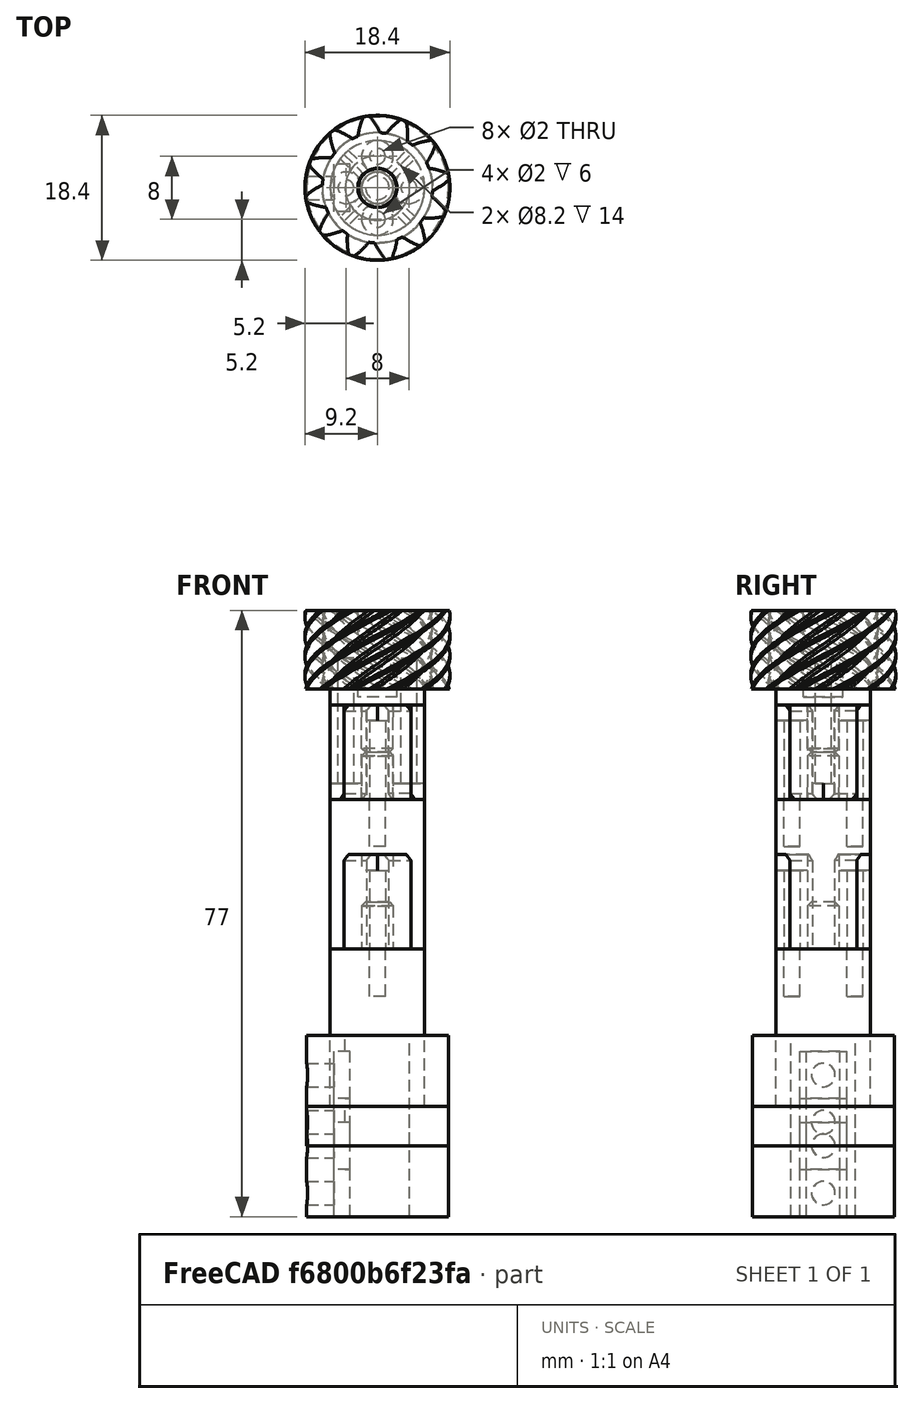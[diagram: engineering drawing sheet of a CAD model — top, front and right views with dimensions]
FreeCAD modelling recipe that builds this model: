
FCSTD DOCUMENT  (FreeCAD 0.19R24276 (Git))
Label: G-midi_inner-gear_002
License: All rights reserved
LicenseURL: http://en.wikipedia.org/wiki/All_rights_reserved
objects: Part::Cylinder×32, Part::Cut×26, Part::Compound×17, Part::Box×10, Part::Chamfer×6, Part::FeaturePython×3
note: 94 computed .brp shape members not serialized (recipe doc carries the construction recipe); baked Part::Feature solids carry a one-line shape summary decoded from their .brp

FEATURE [Part::Cylinder] Cylinder1841  label="Válec1841"
  Angle = 360
  AttacherType = Attacher::AttachEngine3D
  Height = 6
  Placement = pos=(0,0,-14) rot=(0,0,1;0rad)
  Radius = 2
FEATURE [Part::Cylinder] Cylinder1838  label="Válec1838"
  Angle = 360
  AttacherType = Attacher::AttachEngine3D
  Height = 12
  Placement = pos=(0,0,-20) rot=(0,0,1;0rad)
  Radius = 2
FEATURE [Part::Cylinder] Cylinder1839  label="Válec1839"
  Angle = 360
  AttacherType = Attacher::AttachEngine3D
  Height = 12
  Placement = pos=(0,0,-20) rot=(0,0,1;0rad)
  Radius = 6
FEATURE [Part::Cut] Cut392
  Base = -> Cylinder1839
  Tool = -> Cylinder1838
FEATURE [Part::Box] Box369  label="Krychle369"
  AttacherType = Attacher::AttachEngine3D
  Height = 12
  Length = 16
  Placement = pos=(-5.65685,-5.65685,-20) rot=(0,0,1;0.785398rad)
  Width = 8
FEATURE [Part::Cylinder] Cylinder1840  label="Válec1840"
  Angle = 360
  AttacherType = Attacher::AttachEngine3D
  Height = 20
  Placement = pos=(4,0,-20) rot=(0,0,-1;1.5708rad)
  Radius = 1
FEATURE [Part::Box] Box370  label="Krychle370"
  AttacherType = Attacher::AttachEngine3D
  Height = 12
  Length = 16
  Placement = pos=(5.65685,-5.65685,-20) rot=(0,0,1;2.35619rad)
  Width = 8
FEATURE [Part::Cut] Cut393
  Base = -> Cut392
  Tool = -> Box370
FEATURE [Part::Cut] Cut394
  Base = -> Cut393
  Tool = -> Box369
FEATURE [Part::Cut] Cut395
  Base = -> Cut394
  Tool = -> Cylinder1840
FEATURE [Part::Cut] Cut396
  Base = -> Cut394
  Placement = pos=(0,0,0) rot=(0,0,1;3.14159rad)
  Tool = -> Cylinder1840
FEATURE [Part::Compound] Compound584  label="G-midi_sun-sym-mixo"
  Links = -> [Cut395,Cut396,Cylinder1841]
  Placement = pos=(0,0,26) rot=(0,0,1;0rad)
FEATURE [Part::FeaturePython] wormgear061  # WARN: FeaturePython — macro-defined, semantics opaque (R4)
  AttacherType = Attacher::AttachEngine3D
  Placement = pos=(0,0,20) rot=(0,0,1;0.881391rad)
  beta = 30.9638
  clearance = 0.25
  diameter = 16
  head = 0.5
  height = 10
  module = 0.8
  pressure_angle = 20
  reverse_pitch = false
  teeth = 12
  version = 0.0.3
FEATURE [Part::Cylinder] Cylinder  label="Válec"
  Angle = 360
  AttacherType = Attacher::AttachEngine3D
  Height = 2
  Placement = pos=(0,0,18) rot=(0,0,1;0rad)
  Radius = 6
FEATURE [Part::Cylinder] Cylinder031  label="Válec031"
  Angle = 360
  AttacherType = Attacher::AttachEngine3D
  Height = 11
  Placement = pos=(0,0,19) rot=(0,0,1;0rad)
  Radius = 2.5
FEATURE [Part::Compound] Compound
  Links = -> [wormgear061,Cylinder]
FEATURE [Part::Cut] Cut
  Base = -> Compound
  Tool = -> Cylinder031
FEATURE [Part::Cylinder] Cylinder1842  label="Válec1842"
  Angle = 360
  AttacherType = Attacher::AttachEngine3D
  Height = 2
  Placement = pos=(4,0,-20) rot=(0,0,-1;1.5708rad)
  Radius = 2
FEATURE [Part::Cylinder] Cylinder1843  label="Válec1843"
  Angle = 360
  AttacherType = Attacher::AttachEngine3D
  Height = 2
  Placement = pos=(-4,0,-20) rot=(0,0,-1;1.5708rad)
  Radius = 2
FEATURE [Part::Cylinder] Cylinder1844  label="Válec1844"
  Angle = 360
  AttacherType = Attacher::AttachEngine3D
  Height = 20
  Placement = pos=(4,0,-20) rot=(0,0,-1;1.5708rad)
  Radius = 1
FEATURE [Part::Cylinder] Cylinder1845  label="Válec1845"
  Angle = 360
  AttacherType = Attacher::AttachEngine3D
  Height = 20
  Placement = pos=(-4,0,-20) rot=(0,0,-1;1.5708rad)
  Radius = 1
FEATURE [Part::Compound] Compound585
  Links = -> [Cylinder1842,Cylinder1843]
  Placement = pos=(0,0,26) rot=(0,0,1;0rad)
FEATURE [Part::Chamfer] Chamfer
  Base = -> Compound584
  Edges = 4 edges r=0.75: [Edge8,Edge11,Edge29,Edge32]
FEATURE [Part::Cut] Cut397
  Base = -> Chamfer
  Tool = -> Compound585
FEATURE [Part::Compound] Compound586
  Links = -> [Cylinder1844,Cylinder1845]
  Placement = pos=(0,0,24) rot=(0,0,1;0rad)
FEATURE [Part::Cut] Cut398
  Base = -> Cut
  Tool = -> Compound586
FEATURE [Part::Chamfer] Chamfer001
  Base = -> Cut397
  Edges = 1 edges r=0.5: [Edge75]
FEATURE [Part::Compound] Compound587  label="G-midi_inner-gear-part-A"
  Links = -> [Cut398,Chamfer001]
FEATURE [Part::FeaturePython] Tube094  # WARN: FeaturePython — macro-defined, semantics opaque (R4)
  AttacherType = Attacher::AttachEngine3D
  Height = 14
  InnerRadius = 4.1
  OuterRadius = 9
  Placement = pos=(0,0,-100) rot=(0,0,1;0rad)
FEATURE [Part::Cylinder] Cylinder751  label="Válec751"
  Angle = 360
  AttacherType = Attacher::AttachEngine3D
  Height = 10
  Placement = pos=(-11,0,-91) rot=(0.57735,0.57735,0.57735;2.0944rad)
  Radius = 1.5
FEATURE [Part::Cylinder] Cylinder752  label="Válec752"
  Angle = 360
  AttacherType = Attacher::AttachEngine3D
  Height = 10
  Placement = pos=(-11,0,-97) rot=(0.57735,0.57735,0.57735;2.0944rad)
  Radius = 1.5
FEATURE [Part::Compound] Compound533
  Links = -> [Cylinder751,Cylinder752]
FEATURE [Part::Box] Box313  label="Krychle313"
  AttacherType = Attacher::AttachEngine3D
  Height = 6
  Length = 6
  Placement = pos=(-3.5,-3,-100) rot=(0,0,1;1.5708rad)
  Width = 2
FEATURE [Part::Box] Box314  label="Krychle314"
  AttacherType = Attacher::AttachEngine3D
  Height = 6
  Length = 6
  Placement = pos=(-3.5,-3,-94) rot=(0,0,1;1.5708rad)
  Width = 2
FEATURE [Part::Compound] Compound532
  Links = -> [Box313,Box314]
FEATURE [Part::Cut] Cut303
  Base = -> Tube094
  Tool = -> Compound532
FEATURE [Part::Cut] Cut304
  Base = -> Cut303
  Placement = pos=(0,0,53) rot=(0,0,1;0rad)
  Tool = -> Compound533
FEATURE [Part::Cylinder] Cylinder754  label="Válec754"
  Angle = 360
  AttacherType = Attacher::AttachEngine3D
  Height = 20
  Placement = pos=(0,0,-33) rot=(0,0,1;0rad)
  Radius = 6
FEATURE [Part::Cylinder] Cylinder1846  label="Válec1846"
  Angle = 360
  AttacherType = Attacher::AttachEngine3D
  Height = 12
  Placement = pos=(0,0,-20) rot=(0,0,1;0rad)
  Radius = 2
FEATURE [Part::Cylinder] Cylinder1847  label="Válec1847"
  Angle = 360
  AttacherType = Attacher::AttachEngine3D
  Height = 6
  Placement = pos=(0,0,-14) rot=(0,0,1;0rad)
  Radius = 2
FEATURE [Part::Box] Box371  label="Krychle371"
  AttacherType = Attacher::AttachEngine3D
  Height = 12
  Length = 16
  Placement = pos=(-5.65685,-5.65685,-20) rot=(0,0,1;0.785398rad)
  Width = 8
FEATURE [Part::Cylinder] Cylinder1848  label="Válec1848"
  Angle = 360
  AttacherType = Attacher::AttachEngine3D
  Height = 20
  Placement = pos=(4,0,-20) rot=(0,0,-1;1.5708rad)
  Radius = 1
FEATURE [Part::Box] Box372  label="Krychle372"
  AttacherType = Attacher::AttachEngine3D
  Height = 12
  Length = 16
  Placement = pos=(5.65685,-5.65685,-20) rot=(0,0,1;2.35619rad)
  Width = 8
FEATURE [Part::Cylinder] Cylinder1849  label="Válec1849"
  Angle = 360
  AttacherType = Attacher::AttachEngine3D
  Height = 12
  Placement = pos=(0,0,-20) rot=(0,0,1;0rad)
  Radius = 6
FEATURE [Part::Cut] Cut400
  Base = -> Cylinder1849
  Tool = -> Cylinder1846
FEATURE [Part::Cut] Cut404
  Base = -> Cut400
  Tool = -> Box372
FEATURE [Part::Cut] Cut401
  Base = -> Cut404
  Tool = -> Box371
FEATURE [Part::Cut] Cut402
  Base = -> Cut401
  Tool = -> Cylinder1848
FEATURE [Part::Cut] Cut403
  Base = -> Cut401
  Placement = pos=(0,0,0) rot=(0,0,1;3.14159rad)
  Tool = -> Cylinder1848
FEATURE [Part::Compound] Compound588  label="G-midi_sun-sym-mixo001"
  Links = -> [Cut402,Cut403,Cylinder1847]
  Placement = pos=(0,0,26) rot=(0,0,1;0rad)
FEATURE [Part::Chamfer] Chamfer002
  Base = -> Compound588
  Edges = 4 edges r=0.75: [Edge8,Edge11,Edge29,Edge32]
FEATURE [Part::Cylinder] Cylinder1850  label="Válec1850"
  Angle = 360
  AttacherType = Attacher::AttachEngine3D
  Height = 2
  Placement = pos=(-4,0,-20) rot=(0,0,-1;1.5708rad)
  Radius = 2
FEATURE [Part::Cylinder] Cylinder1851  label="Válec1851"
  Angle = 360
  AttacherType = Attacher::AttachEngine3D
  Height = 2
  Placement = pos=(4,0,-20) rot=(0,0,-1;1.5708rad)
  Radius = 2
FEATURE [Part::Compound] Compound589
  Links = -> [Cylinder1851,Cylinder1850]
  Placement = pos=(0,0,26) rot=(0,0,1;0rad)
FEATURE [Part::Cut] Cut399
  Base = -> Chamfer002
  Tool = -> Compound589
FEATURE [Part::Chamfer] Chamfer003
  Base = -> Cut399
  Edges = 1 edges r=0.5: [Edge75]
  Placement = pos=(0,0,5) rot=(0.707107,0.707107,0;3.14159rad)
FEATURE [Part::Cylinder] Cylinder1852  label="Válec1852"
  Angle = 360
  AttacherType = Attacher::AttachEngine3D
  Height = 20
  Placement = pos=(4,0,-20) rot=(0,0,-1;1.5708rad)
  Radius = 1
FEATURE [Part::Cylinder] Cylinder1853  label="Válec1853"
  Angle = 360
  AttacherType = Attacher::AttachEngine3D
  Height = 20
  Placement = pos=(-4,0,-20) rot=(0,0,-1;1.5708rad)
  Radius = 1
FEATURE [Part::Compound] Compound590
  Links = -> [Cylinder1852,Cylinder1853]
  Placement = pos=(0,0,1) rot=(0,0,1;1.5708rad)
FEATURE [Part::Cut] Cut405
  Base = -> Cylinder754
  Tool = -> Compound590
FEATURE [Part::Compound] Compound591  label="G-midi_inner-gear-part-B"
  Links = -> [Cut304,Chamfer003,Cut405]
FEATURE [Part::Box] Box396  label="Krychle396"
  AttacherType = Attacher::AttachEngine3D
  Height = 12
  Length = 16
  Placement = pos=(-5.65685,-5.65685,-20) rot=(0,0,1;0.785398rad)
  Width = 8
FEATURE [Part::Cylinder] Cylinder1943  label="Válec1943"
  Angle = 360
  AttacherType = Attacher::AttachEngine3D
  Height = 20
  Placement = pos=(4,0,-20) rot=(0,0,-1;1.5708rad)
  Radius = 1
FEATURE [Part::Box] Box397  label="Krychle397"
  AttacherType = Attacher::AttachEngine3D
  Height = 6
  Length = 6
  Placement = pos=(-3.5,-3,-94) rot=(0,0,1;1.5708rad)
  Width = 2
FEATURE [Part::Cylinder] Cylinder1944  label="Válec1944"
  Angle = 360
  AttacherType = Attacher::AttachEngine3D
  Height = 2
  Placement = pos=(4,0,-20) rot=(0,0,-1;1.5708rad)
  Radius = 2
FEATURE [Part::Cylinder] Cylinder1945  label="Válec1945"
  Angle = 360
  AttacherType = Attacher::AttachEngine3D
  Height = 2
  Placement = pos=(-4,0,-20) rot=(0,0,-1;1.5708rad)
  Radius = 2
FEATURE [Part::Compound] Compound626
  Links = -> [Cylinder1944,Cylinder1945]
  Placement = pos=(0,0,26) rot=(0,0,1;0rad)
FEATURE [Part::Cylinder] Cylinder1946  label="Válec1946"
  Angle = 360
  AttacherType = Attacher::AttachEngine3D
  Height = 10
  Placement = pos=(-11,0,-97) rot=(0.57735,0.57735,0.57735;2.0944rad)
  Radius = 1.5
FEATURE [Part::Cylinder] Cylinder1941  label="Válec1941"
  Angle = 360
  AttacherType = Attacher::AttachEngine3D
  Height = 12
  Placement = pos=(0,0,-20) rot=(0,0,1;0rad)
  Radius = 6
FEATURE [Part::Cylinder] Cylinder1947  label="Válec1947"
  Angle = 360
  AttacherType = Attacher::AttachEngine3D
  Height = 10
  Placement = pos=(-11,0,-91) rot=(0.57735,0.57735,0.57735;2.0944rad)
  Radius = 1.5
FEATURE [Part::Compound] Compound623
  Links = -> [Cylinder1947,Cylinder1946]
FEATURE [Part::Cylinder] Cylinder1937  label="Válec1937"
  Angle = 360
  AttacherType = Attacher::AttachEngine3D
  Height = 30
  Placement = pos=(0,0,-43) rot=(0,0,1;0rad)
  Radius = 6
FEATURE [Part::Cylinder] Cylinder1938  label="Válec1938"
  Angle = 360
  AttacherType = Attacher::AttachEngine3D
  Height = 6
  Placement = pos=(0,0,-14) rot=(0,0,1;0rad)
  Radius = 2
FEATURE [Part::Cylinder] Cylinder1940  label="Válec1940"
  Angle = 360
  AttacherType = Attacher::AttachEngine3D
  Height = 20
  Placement = pos=(4,0,-20) rot=(0,0,-1;1.5708rad)
  Radius = 1
FEATURE [Part::Cylinder] Cylinder1939  label="Válec1939"
  Angle = 360
  AttacherType = Attacher::AttachEngine3D
  Height = 12
  Placement = pos=(0,0,-20) rot=(0,0,1;0rad)
  Radius = 2
FEATURE [Part::Cut] Cut448
  Base = -> Cylinder1941
  Tool = -> Cylinder1939
FEATURE [Part::Box] Box394  label="Krychle394"
  AttacherType = Attacher::AttachEngine3D
  Height = 6
  Length = 6
  Placement = pos=(-3.5,-3,-100) rot=(0,0,1;1.5708rad)
  Width = 2
FEATURE [Part::Compound] Compound624
  Links = -> [Box394,Box397]
FEATURE [Part::Cylinder] Cylinder1942  label="Válec1942"
  Angle = 360
  AttacherType = Attacher::AttachEngine3D
  Height = 20
  Placement = pos=(-4,0,-20) rot=(0,0,-1;1.5708rad)
  Radius = 1
FEATURE [Part::Compound] Compound628
  Links = -> [Cylinder1943,Cylinder1942]
  Placement = pos=(0,0,1) rot=(0,0,1;1.5708rad)
FEATURE [Part::Cut] Cut444
  Base = -> Cylinder1937
  Tool = -> Compound628
FEATURE [Part::Box] Box395  label="Krychle395"
  AttacherType = Attacher::AttachEngine3D
  Height = 12
  Length = 16
  Placement = pos=(5.65685,-5.65685,-20) rot=(0,0,1;2.35619rad)
  Width = 8
FEATURE [Part::Cut] Cut451
  Base = -> Cut448
  Tool = -> Box395
FEATURE [Part::Cut] Cut449
  Base = -> Cut451
  Tool = -> Box396
FEATURE [Part::Cut] Cut450
  Base = -> Cut449
  Placement = pos=(0,0,0) rot=(0,0,1;3.14159rad)
  Tool = -> Cylinder1940
FEATURE [Part::Cut] Cut452
  Base = -> Cut449
  Tool = -> Cylinder1940
FEATURE [Part::Compound] Compound627  label="G-midi_sun-sym-mixo003"
  Links = -> [Cut452,Cut450,Cylinder1938]
  Placement = pos=(0,0,26) rot=(0,0,1;0rad)
FEATURE [Part::Chamfer] Chamfer016
  Base = -> Compound627
  Edges = 4 edges r=0.75: [Edge8,Edge11,Edge29,Edge32]
FEATURE [Part::Cut] Cut447
  Base = -> Chamfer016
  Tool = -> Compound626
FEATURE [Part::Chamfer] Chamfer017
  Base = -> Cut447
  Edges = 1 edges r=0.5: [Edge75]
  Placement = pos=(0,0,5) rot=(0.707107,0.707107,0;3.14159rad)
FEATURE [Part::FeaturePython] Tube095  # WARN: FeaturePython — macro-defined, semantics opaque (R4)
  AttacherType = Attacher::AttachEngine3D
  Height = 14
  InnerRadius = 4.1
  OuterRadius = 9
  Placement = pos=(0,0,-100) rot=(0,0,1;0rad)
FEATURE [Part::Cut] Cut445
  Base = -> Tube095
  Tool = -> Compound624
FEATURE [Part::Cut] Cut446
  Base = -> Cut445
  Placement = pos=(0,0,43) rot=(0,0,1;0rad)
  Tool = -> Compound623
FEATURE [Part::Compound] Compound625  label="G-midi_inner-gear-part-B_proper-lenght"
  Links = -> [Cut446,Chamfer017,Cut444]
  Placement = pos=(0,0,19) rot=(0,0,1;0rad)
